# Revit family: LG_VRF_HR_Unit_Serial3_4_Port_v1.1
name_source: partatom
category: Mechanical Equipment
units: mm (PartAtom-declared; Revit-internal decimal feet)

## family parameters
Always vertical = Yes
Cut with Voids When Loaded = No
OmniClass Number = 23.75.00.00
OmniClass Title = Climate Control (HVAC)
Part Type = Normal
Room Calculation Point = No
Round Connector Dimension = Use Radius
Shared = No
Work Plane-Based = No

## types (2) — shared parameters
Default Elevation = 0"
Diameter Gas Front Out1 = 15.88 mm
Diameter Gas Front Out1 outline = 3/4"
Diameter Gas Front Out2 = 15.88 mm
Diameter Gas Front Out2 outline = 3/4"
Diameter Gas Front Out3 = 15.88 mm
Diameter Gas Front Out3 outline = 3/4"
Diameter Gas Front Out4 = 15.88 mm
Diameter Gas Front Out4 outline = 3/4"
Diameter Gas Front Out5 = 5/8"
Diameter Gas Front Out5 outline = 3/4"
Diameter Gas Front Out6 = 5/8"
Diameter Gas Front Out6 outline = 3/4"
Diameter Gas Front Out7 = 5/8"
Diameter Gas Front Out7 outline = 3/4"
Diameter Gas Front Out8 = 5/8"
Diameter Gas Front Out8 outline = 3/4"
Diameter Gas_Low In = 28.58 mm
Diameter Gas_Low In outline = 1 1/4"
Diameter Gas_Low Out = 28.58 mm
Diameter Gas_Low Out outline = 1 1/4"
Diameter Gas_high In = 22.20 mm
Diameter Gas_high In outline = 1"
Diameter Gas_high Out = 22.20 mm
Diameter Gas_high Out outline = 1"
Diameter Liquid Front Out1 = 9.52 mm
Diameter Liquid Front Out1 outline = 1/2"
Diameter Liquid Front Out2 = 9.52 mm
Diameter Liquid Front Out2 outline = 1/2"
Diameter Liquid Front Out3 = 9.52 mm
Diameter Liquid Front Out3 outline = 1/2"
Diameter Liquid Front Out4 = 9.52 mm
Diameter Liquid Front Out4 outline = 1/2"
Diameter Liquid Front Out5 = 3/8"
Diameter Liquid Front Out5 outline = 1/2"
Diameter Liquid Front Out6 = 3/8"
Diameter Liquid Front Out6 outline = 1/2"
Diameter Liquid Front Out7 = 3/8"
Diameter Liquid Front Out7 outline = 1/2"
Diameter Liquid Front Out8 = 3/8"
Diameter Liquid Front Out8 outline = 1/2"
Diameter Liquid In = 15.88 mm
Diameter Liquid In outline = 3/4"
Diameter Liquid Out = 15.88 mm
Diameter Liquid Out outline = 3/4"
Hanger offset height = 1 7/16"
Hanger offset mid = 12 1/4"
Hanger offset side = 3 13/16"
Height offset Gas front = 3 9/16"
Height offset Gas_High side = 3 9/16"
Height offset Gas_Low side = 5 1/2"
Height offset Liquid front = 3/4"
Height offset Liquid side = 5 1/2"
Height offset side = 3/16"
Lenght pipe mid = 3 3/16"
Lenght pipe side = 4 1/4"
Length = 31 1/4"
Length offset front pipe = 6 15/16"
Length offset front pipe mid = 6 9/16"
Length offset left pipe = 6 5/16"
Length offset left pipe mid = 5 1/8"
Length offset right pipe = 6 5/16"
Length offset right pipe mid = 5 7/8"
Length offset side = 3/16"
Manufacturer = LG Electronics
Width = 18 15/16"
Width offset Gas_High = 13 1/16"
Width offset Gas_Low = 11 11/16"
Width offset Liquid = 14 1/8"
Width offset back = 2 3/8"
Width offset back side = 3/8"

## per-type parameters (varying)
| type | Height |
| PRHR043 | 8 9/16" |
| PRHR043A | 8 5/8" |

note: column(s) folded — value = type name in every type: Model

## geometry (parser evidence)
native form markers: Sweep x2
no freeform markers — native parametric forms only
